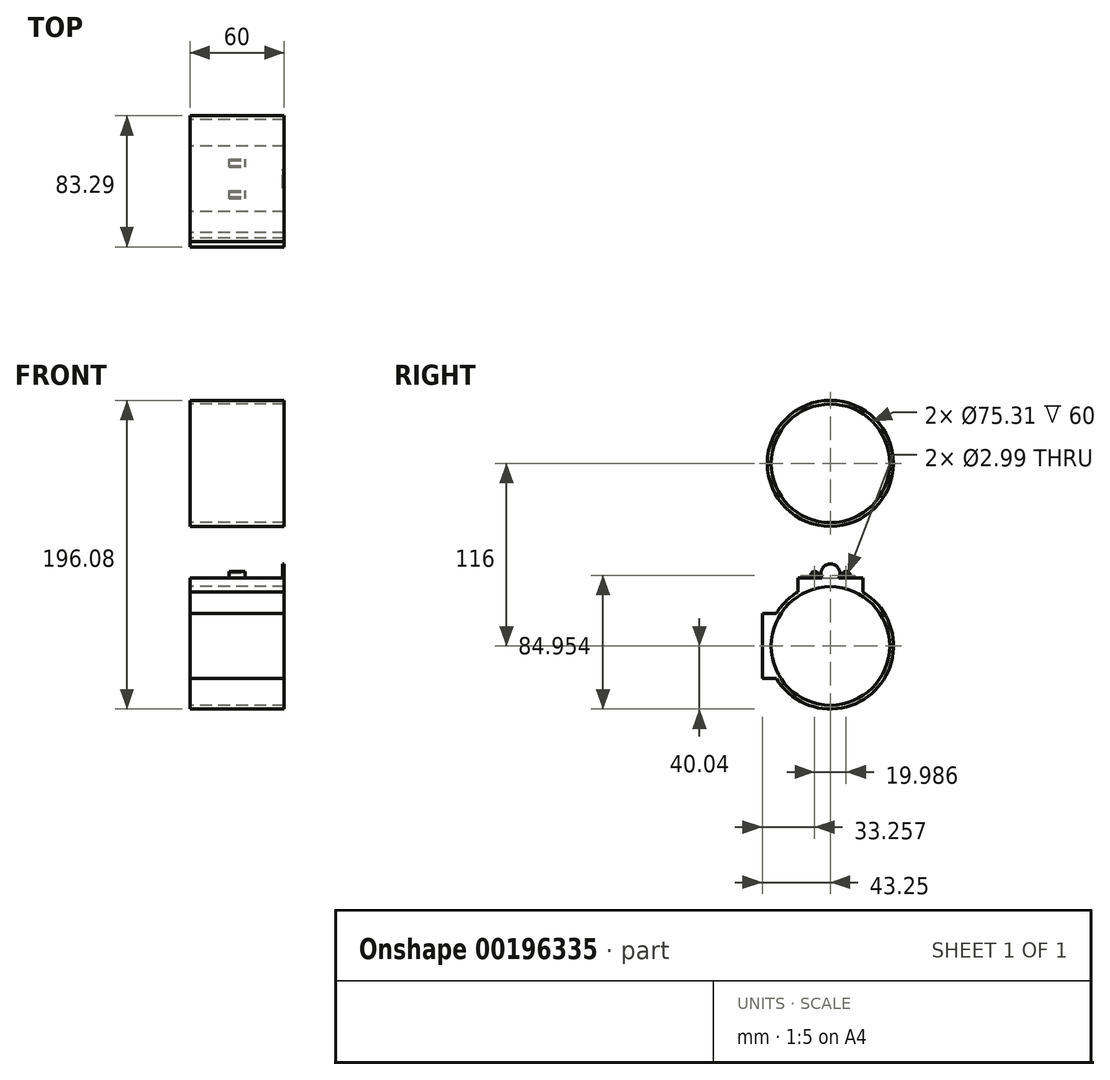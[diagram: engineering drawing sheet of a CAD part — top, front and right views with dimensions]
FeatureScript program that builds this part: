
annotation { "Feature Type Name" : "Feature", "Feature Type Description" : "" }
export const myFeature = defineFeature(function(context is Context, id is Id, definition is map)
    precondition{}
    {
        {
            var Q0;
            Q0=qCreatedBy(makeId("Right.planeOp"),FACE);
            var sketch = newSketch(context, id + "F0", { "sketchPlane" : qUnion([Q0])});
            skCircle(sketch, "E0", {"center": v(0, 0) * mm, "radius": 40.04 * mm});
            skSolve(sketch);
        }
        {
            var Q0;
            Q0 = qSketchRegion(id + "F0", true);
            extrude(context, id + "F1", {"entities" : qUnion([Q0]), "depth" : 60 * mm});
        }
        {
            var Q0;
            Q0=qCreatedBy(makeId("Right.planeOp"),FACE);
            var sketch = newSketch(context, id + "F2", { "sketchPlane" : qUnion([Q0])});
            skCircle(sketch, "E1", {"center": v(0, 0) * mm, "radius": 37.66 * mm});
            skSolve(sketch);
        }
        {
            var Q0;
            Q0 = qSketchRegion(id + "F2", true);
            extrude(context, id + "F3", {"entities" : qUnion([Q0]), "operationType" : NewBodyOperationType.REMOVE, "depth" : 120 * mm});
        }
        {
            var Q0;
            Q0=qCreatedBy(makeId("Right.planeOp"),FACE);
            var sketch = newSketch(context, id + "F4", { "sketchPlane" : qUnion([Q0])});
            skLineSegment(sketch, "E2", {"start": v(0, 43.2) * mm, "end": v(20.75, 43.2) * mm});
            skLineSegment(sketch, "E3", {"start": v(20.75, 43.2) * mm, "end": v(-20.75, 43.2) * mm});
            skArc(sketch, "E4", {"start": v(20.75, 34.19) * mm, "mid": v(0, 40) * mm, "end": v(-20.75, 34.19) * mm});
            skLineSegment(sketch, "E5", {"start": v(20.75, 43.2) * mm, "end": v(20.75, 34.19) * mm});
            skLineSegment(sketch, "E6", {"start": v(-20.75, 43.2) * mm, "end": v(-20.75, 34.19) * mm});
            skSolve(sketch);
        }
        {
            var Q0;
            Q0=makeQuery(id+"F1.opExtrude","SWEPT_BODY",BODY,{"disambiguationData":[OSD([sQuery(id+"F0.wireOp",EDGE,"E0")])]});
            transform(context, id + "F5", {"entities" : qUnion([Q0]), "transformType" : TransformType.TRANSLATION_3D, "dx" : 0 * mm, "dy" : 0 * mm, "dz" : 116 * mm, "makeCopy" : true});
        }
        {
            var Q0;
            Q0 = qSketchRegion(id + "F4", true);
            extrude(context, id + "F6", {"entities" : qUnion([Q0]), "operationType" : NewBodyOperationType.ADD, "depth" : 60 * mm});
        }
        {
            var Q0;
            Q0=makeQuery(id+"F6.opExtrude","CAP_FACE",FACE,{"disambiguationData":[OSD([sQuery(id+"F4.wireOp",EDGE,"E3"),sQuery(id+"F4.wireOp",EDGE,"E4"),sQuery(id+"F4.wireOp",EDGE,"E5"),sQuery(id+"F4.wireOp",EDGE,"E6")])],"isStart":false});
            var sketch = newSketch(context, id + "F7", { "sketchPlane" : qUnion([Q0])});
            skLineSegment(sketch, "E7", {"start": v(0, 40.04) * mm, "end": v(0, 46.07) * mm});
            skPoint(sketch, "E7.endSnap0", {"position": v(0, 40.04) * mm});
            skCircle(sketch, "E8", {"center": v(0, 46.07) * mm, "radius": 6.04 * mm});
            skSolve(sketch);
        }
        {
            var Q0;
            {var subQ0=sQuery(id+"F7.wireOp",EDGE,"E8");var subQ1=makeQuery(id+"F6.opExtrude","CAP_EDGE",EDGE,{"disambiguationData":[OSD([sQuery(id+"F4.wireOp",EDGE,"E3")])],"isStart":false});var subQ2=makeQuery(id+"F7.imprint","INTERSECT",VERTEX,{"disambiguationData":[OD(0.0)],"derivedFrom":[subQ1,subQ0]});Q0=makeQuery(id+"F7.imprint","IMPRINT",FACE,{"disambiguationData":[TD([[makeQuery(id+"F7.imprint","IMPRINT",EDGE,{"disambiguationData":[TD([[subQ2,1.0]])],"derivedFrom":subQ0}),1.0]])]});}
            var Q1;
            {var subQ1=sQuery(id+"F7.wireOp",EDGE,"E7");var subQ2=sQuery(id+"F4.wireOp",EDGE,"E3");var subQ4=makeQuery(id+"F6.opExtrude","CAP_EDGE",EDGE,{"disambiguationData":[OSD([subQ2])],"isStart":false});var subQ5=makeQuery(id+"F7.imprint","INTERSECT",VERTEX,{"derivedFrom":[subQ4,subQ1]});Q1=makeQuery(id+"F7.imprint","IMPRINT",FACE,{"disambiguationData":[TD([[makeQuery(id+"F7.imprint","IMPRINT",EDGE,{"disambiguationData":[TD([[subQ5,-1.0]])],"derivedFrom":subQ4}),1.0]])]});}
            var Q2;
            {var subQ1=sQuery(id+"F7.wireOp",EDGE,"E7");var subQ2=sQuery(id+"F4.wireOp",EDGE,"E3");var subQ4=makeQuery(id+"F6.opExtrude","CAP_EDGE",EDGE,{"disambiguationData":[OSD([subQ2])],"isStart":false});var subQ5=makeQuery(id+"F7.imprint","INTERSECT",VERTEX,{"derivedFrom":[subQ4,subQ1]});Q2=makeQuery(id+"F7.imprint","IMPRINT",FACE,{"disambiguationData":[TD([[makeQuery(id+"F7.imprint","IMPRINT",EDGE,{"disambiguationData":[TD([[subQ5,1.0]])],"derivedFrom":subQ4}),1.0]])]});}
            extrude(context, id + "F8", {"entities" : qUnion([Q0, Q1, Q2]), "operationType" : NewBodyOperationType.ADD, "oppositeDirection" : true, "depth" : 1 * mm});
        }
        {
            var Q0;
            Q0=qCreatedBy(makeId("Right.planeOp"),FACE);
            cPlane(context, id + "F9", {"entities" : qUnion([Q0]), "cplaneType" : CPlaneType.OFFSET, "offset" : 35 * mm, "width" : 150 * mm, "height" : 150 * mm});
        }
        {
            var Q0;
            Q0=qCreatedBy(id+"F9.planeOp",FACE);
            var sketch = newSketch(context, id + "F10", { "sketchPlane" : qUnion([Q0])});
            skCircle(sketch, "E9", {"center": v(-10, 44.91) * mm, "radius": 2.5 * mm});
            skCircle(sketch, "E10.MirrorC", {"center": v(10, 44.91) * mm, "radius": 2.5 * mm});
            skSolve(sketch);
        }
        {
            var Q0;
            Q0 = qSketchRegion(id + "F10", true);
            extrude(context, id + "F11", {"entities" : qUnion([Q0]), "operationType" : NewBodyOperationType.ADD, "oppositeDirection" : true, "depth" : 10 * mm});
        }
        {
            var Q0;
            Q0=makeQuery(id+"F11.opExtrude","CAP_FACE",FACE,{"disambiguationData":[OSD([sQuery(id+"F10.wireOp",EDGE,"E9")])],"isStart":true});
            var sketch = newSketch(context, id + "F12", { "sketchPlane" : qUnion([Q0])});
            skCircle(sketch, "E11", {"center": v(-10, 44.91) * mm, "radius": 1.5 * mm});
            skCircle(sketch, "E12.MirrorC", {"center": v(10, 44.91) * mm, "radius": 1.5 * mm});
            skSolve(sketch);
        }
        {
            var Q0;
            Q0 = qSketchRegion(id + "F12", true);
            extrude(context, id + "F13", {"entities" : qUnion([Q0]), "operationType" : NewBodyOperationType.REMOVE, "oppositeDirection" : true, "depth" : 10 * mm});
        }
        {
            var Q0;
            Q0=makeQuery(id+"F6.boolean.opBoolean","MERGE",FACE,{"derivedFrom":[makeQuery(id+"F1.opExtrude","CAP_FACE",FACE,{"disambiguationData":[OSD([sQuery(id+"F0.wireOp",EDGE,"E0")])],"isStart":true}),makeQuery(id+"F6.opExtrude","CAP_FACE",FACE,{"disambiguationData":[OSD([sQuery(id+"F4.wireOp",EDGE,"E3"),sQuery(id+"F4.wireOp",EDGE,"E4"),sQuery(id+"F4.wireOp",EDGE,"E5"),sQuery(id+"F4.wireOp",EDGE,"E6")])],"isStart":true})]});
            var sketch = newSketch(context, id + "F14", { "sketchPlane" : qUnion([Q0])});
            skLineSegment(sketch, "E13", {"start": v(43.25, 0) * mm, "end": v(43.25, 20.75) * mm});
            skLineSegment(sketch, "E14.MirrorCS", {"start": v(43.25, 0) * mm, "end": v(43.25, -20.75) * mm});
            skLineSegment(sketch, "E15", {"start": v(43.25, -20.75) * mm, "end": v(34.24, -20.75) * mm});
            skLineSegment(sketch, "E16", {"start": v(43.25, 20.75) * mm, "end": v(34.24, 20.75) * mm});
            skArc(sketch, "E17", {"start": v(34.24, -20.75) * mm, "mid": v(40.04, 0) * mm, "end": v(34.24, 20.75) * mm});
            skPoint(sketch, "E18.start.orphan", {"position": v(40.04, 0) * mm});
            skSolve(sketch);
        }
        {
            var Q0;
            Q0=makeQuery(id+"F14.imprint","IMPRINT",FACE,{"disambiguationData":[TD([[makeQuery(id+"F14.imprint","IMPRINT",EDGE,{"derivedFrom":sQuery(id+"F14.wireOp",EDGE,"E13")}),1.0]])]});
            extrude(context, id + "F15", {"entities" : qUnion([Q0]), "operationType" : NewBodyOperationType.ADD, "oppositeDirection" : true, "depth" : 60 * mm});
        }
    });
